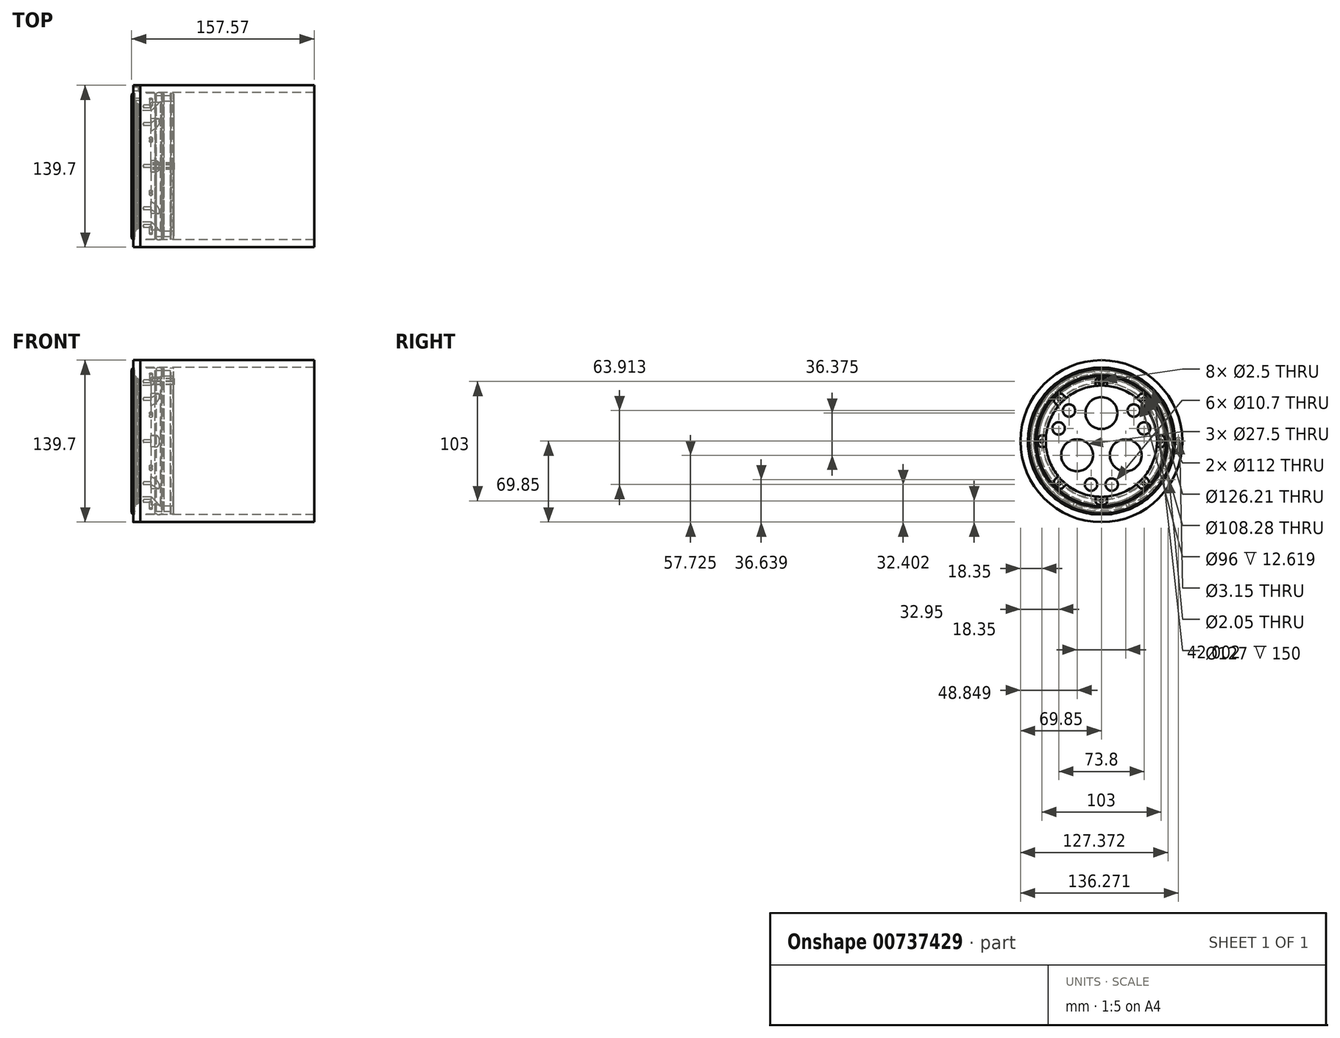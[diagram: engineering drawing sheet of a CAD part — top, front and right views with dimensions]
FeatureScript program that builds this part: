
annotation { "Feature Type Name" : "Feature", "Feature Type Description" : "" }
export const myFeature = defineFeature(function(context is Context, id is Id, definition is map)
    precondition{}
    {
        {
            assignVariable(context, id + "F0", {"name" : "M3_Helicoil_Drill_Depth", "anyValue" : 6.5});
        }
        {
            var Q0;
            Q0=qCreatedBy(makeId("Front.planeOp"),FACE);
            var sketch = newSketch(context, id + "F1", { "sketchPlane" : qUnion([Q0])});
            skLineSegment(sketch, "E0", {"start": v(0, 69.85) * mm, "end": v(6.25, 69.85) * mm});
            skLineSegment(sketch, "E1", {"start": v(6.25, 69.85) * mm, "end": v(6.25, 63) * mm});
            skLineSegment(sketch, "E2", {"start": v(6.25, 63) * mm, "end": v(35, 63) * mm, "construction": true});
            skLineSegment(sketch, "E3", {"start": v(35, 63) * mm, "end": v(35, 56) * mm});
            skLineSegment(sketch, "E4", {"start": v(35, 56) * mm, "end": v(23.5, 56) * mm});
            skLineSegment(sketch, "E5", {"start": v(23.5, 56) * mm, "end": v(15.5, 48) * mm});
            skLineSegment(sketch, "E6", {"start": v(15.5, 48) * mm, "end": v(2.38, 48) * mm});
            skLineSegment(sketch, "E7", {"start": v(2.38, 48) * mm, "end": v(2.38, 56) * mm, "construction": true});
            skLineSegment(sketch, "E8", {"start": v(2.38, 56) * mm, "end": v(0, 56) * mm});
            skLineSegment(sketch, "E9", {"start": v(0, 56) * mm, "end": v(0, 69.85) * mm, "construction": true});
            skLineSegment(sketch, "E10", {"start": v(6.25, 63) * mm, "end": v(19, 63) * mm});
            skLineSegment(sketch, "E11", {"start": v(19, 63) * mm, "end": v(19, 60.83) * mm});
            skLineSegment(sketch, "E12", {"start": v(19, 60.83) * mm, "end": v(24.54, 60.83) * mm});
            skLineSegment(sketch, "E13", {"start": v(24.54, 60.83) * mm, "end": v(24.54, 63) * mm});
            skLineSegment(sketch, "E14", {"start": v(24.54, 63) * mm, "end": v(25.54, 63) * mm});
            skLineSegment(sketch, "E15", {"start": v(25.54, 63) * mm, "end": v(25.54, 56) * mm, "construction": true});
            skLineSegment(sketch, "E16.MirrorCS", {"start": v(26.54, 63) * mm, "end": v(25.54, 63) * mm});
            skLineSegment(sketch, "E17.MirrorCS", {"start": v(26.54, 60.83) * mm, "end": v(26.54, 63) * mm});
            skLineSegment(sketch, "E18.MirrorCS", {"start": v(32.07, 60.83) * mm, "end": v(26.54, 60.83) * mm});
            skLineSegment(sketch, "E19.MirrorCS", {"start": v(32.07, 63) * mm, "end": v(32.07, 60.83) * mm});
            skLineSegment(sketch, "E20", {"start": v(32.07, 63) * mm, "end": v(35, 63) * mm});
            skLineSegment(sketch, "E21", {"start": v(0, 0) * mm, "end": v(57.37, 0) * mm, "construction": true});
            skLineSegment(sketch, "E22", {"start": v(0, 69.85) * mm, "end": v(0, 63.1) * mm});
            skLineSegment(sketch, "E23", {"start": v(0, 63.1) * mm, "end": v(1.32, 63.1) * mm});
            skLineSegment(sketch, "E24", {"start": v(1.32, 63.1) * mm, "end": v(1.32, 58.53) * mm});
            skLineSegment(sketch, "E25", {"start": v(1.32, 58.53) * mm, "end": v(0, 58.53) * mm});
            skLineSegment(sketch, "E26", {"start": v(0, 58.53) * mm, "end": v(0, 56) * mm});
            skLineSegment(sketch, "E27", {"start": v(2.38, 48) * mm, "end": v(2.38, 50.63) * mm});
            skLineSegment(sketch, "E28", {"start": v(2.38, 50.63) * mm, "end": v(4.31, 50.63) * mm});
            skLineSegment(sketch, "E29", {"start": v(4.31, 50.63) * mm, "end": v(4.31, 54.14) * mm});
            skLineSegment(sketch, "E30", {"start": v(4.31, 54.14) * mm, "end": v(2.38, 54.14) * mm});
            skLineSegment(sketch, "E31", {"start": v(2.38, 54.14) * mm, "end": v(2.38, 56) * mm});
            skLineSegment(sketch, "E32", {"start": v(-1, 89.78) * mm, "end": v(37.1, 89.78) * mm, "construction": true});
            skSolve(sketch);
        }
        {
            var Q0;
            Q0=qSketchRegion(id+"F1",true);
            var Q1;
            Q1=sQuery(id+"F1.wireOp",EDGE,"E21");
            revolve(context, id + "F2", {"entities" : qUnion([Q0]), "axis" : qUnion([Q1]), "revolveType" : RevolveType.FULL});
        }
        {
            var Q0;
            Q0=makeQuery(id+"F2.opRevolve","SWEPT_FACE",FACE,{"disambiguationData":[OSD([sQuery(id+"F1.wireOp",EDGE,"E1")])]});
            var sketch = newSketch(context, id + "F3", { "sketchPlane" : qUnion([Q0])});
            skCircle(sketch, "E33", {"center": v(0, 0) * mm, "radius": 66.42 * mm, "construction": true});
            skLineSegment(sketch, "E34", {"start": v(0, 0) * mm, "end": v(66.42, 0) * mm, "construction": true});
            skLineSegment(sketch, "E35.1.0", {"start": v(0, 0) * mm, "end": v(57.52, 33.21) * mm, "construction": true});
            skLineSegment(sketch, "E35.2.0", {"start": v(0, 0) * mm, "end": v(33.21, 57.52) * mm, "construction": true});
            skLineSegment(sketch, "E36.1.3.0", {"start": v(0, 0) * mm, "end": v(0, 66.42) * mm, "construction": true});
            skLineSegment(sketch, "E36.1.4.0", {"start": v(0, 0) * mm, "end": v(-33.21, 57.52) * mm, "construction": true});
            skLineSegment(sketch, "E36.1.5.0", {"start": v(0, 0) * mm, "end": v(-57.52, 33.21) * mm, "construction": true});
            skLineSegment(sketch, "E37.1.6.0", {"start": v(0, 0) * mm, "end": v(-66.42, 0) * mm, "construction": true});
            skLineSegment(sketch, "E37.1.7.0", {"start": v(0, 0) * mm, "end": v(-57.52, -33.21) * mm, "construction": true});
            skLineSegment(sketch, "E38.1.8.0", {"start": v(0, 0) * mm, "end": v(-33.21, -57.52) * mm, "construction": true});
            skLineSegment(sketch, "E38.1.9.0", {"start": v(0, 0) * mm, "end": v(0, -66.42) * mm, "construction": true});
            skLineSegment(sketch, "E38.1.10.0", {"start": v(0, 0) * mm, "end": v(33.21, -57.52) * mm, "construction": true});
            skLineSegment(sketch, "E38.1.11.0", {"start": v(0, 0) * mm, "end": v(57.52, -33.21) * mm, "construction": true});
            skLineSegment(sketch, "E39", {"start": v(69.85, 0) * mm, "end": v(63, 0) * mm, "construction": true});
            skSolve(sketch);
        }
        {
            var Q0;
            Q0=qCreatedBy(makeId("Top.planeOp"),FACE);
            var Q1;
            Q1=sQuery(id+"F1.wireOp",VERTEX,"E10.end");
            cPlane(context, id + "F4", {"entities" : qUnion([Q0, Q1]), "cplaneType" : CPlaneType.PLANE_POINT, "offset" : 150 * mm, "width" : 150 * mm, "height" : 150 * mm});
        }
        {
            var Q0;
            Q0=qCreatedBy(id+"F4.planeOp",FACE);
            var sketch = newSketch(context, id + "F5", { "sketchPlane" : qUnion([Q0])});
            skPoint(sketch, "E40", {"position": v(15.25, 0) * mm});
            skLineSegment(sketch, "E41.0", {"start": v(6.25, -69.85) * mm, "end": v(6.25, 69.85) * mm, "construction": true});
            skLineSegment(sketch, "E41.1", {"start": v(19, -63) * mm, "end": v(19, 63) * mm, "construction": true});
            skLineSegment(sketch, "E42", {"start": v(6.25, 0) * mm, "end": v(19, 0) * mm, "construction": true});
            skCircle(sketch, "E43", {"center": v(15.25, 0) * mm, "radius": 1.5 * mm, "construction": true});
            skCircle(sketch, "E44", {"center": v(15.25, 0) * mm, "radius": 2.75 * mm, "construction": true});
            skSolve(sketch);
        }
        {
            var Q0;
            Q0=makeQuery(id+"F2.opRevolve","SWEPT_EDGE",EDGE,{"disambiguationData":[OSD([sQuery(id+"F1.wireOp",EDGE,"E3"),sQuery(id+"F1.wireOp",EDGE,"E20")])]});
            chamfer(context, id + "F6", {"entities" : qUnion([Q0]), "chamferType" : ChamferType.OFFSET_ANGLE, "width" : 2 * mm, "oppositeDirection" : false, "angle" : 10 * degree, "tangentPropagation" : true});
        }
        {
            var Q0;
            Q0=makeQuery(id+"F2.opRevolve","SWEPT_EDGE",EDGE,{"disambiguationData":[OSD([sQuery(id+"F1.wireOp",EDGE,"E8"),sQuery(id+"F1.wireOp",EDGE,"E26")])]});
            var Q1;
            Q1=makeQuery(id+"F2.opRevolve","SWEPT_EDGE",EDGE,{"disambiguationData":[OSD([sQuery(id+"F1.wireOp",EDGE,"E6"),sQuery(id+"F1.wireOp",EDGE,"E27")])]});
            chamfer(context, id + "F7", {"entities" : qUnion([Q0, Q1]), "width" : .5 * mm, "tangentPropagation" : true});
        }
        {
            var Q0;
            Q0=makeQuery(id+"F2.opRevolve","SWEPT_EDGE",EDGE,{"disambiguationData":[OSD([sQuery(id+"F1.wireOp",EDGE,"E3"),sQuery(id+"F1.wireOp",EDGE,"E4")])]});
            chamfer(context, id + "F8", {"entities" : qUnion([Q0]), "width" : 1 * mm, "tangentPropagation" : true});
        }
        {
            var Q0;
            Q0=makeQuery(id+"F2.opRevolve","SWEPT_FACE",FACE,{"disambiguationData":[OSD([sQuery(id+"F1.wireOp",EDGE,"E24")])]});
            fillet(context, id + "F9", {"entities" : qUnion([Q0]), "radius" : 0.2 * mm, "tangentPropagation" : true, "allowEdgeOverflow" : false});
        }
        {
            var Q0;
            Q0=makeQuery(id+"F2.opRevolve","SWEPT_FACE",FACE,{"disambiguationData":[OSD([sQuery(id+"F1.wireOp",EDGE,"E29")])]});
            fillet(context, id + "F10", {"entities" : qUnion([Q0]), "radius" : 0.2 * mm, "allowEdgeOverflow" : false});
        }
        {
            var Q0;
            Q0=makeQuery(id+"F2.opRevolve","SWEPT_FACE",FACE,{"disambiguationData":[OSD([sQuery(id+"F1.wireOp",EDGE,"E18.MirrorCS")])]});
            var Q1;
            Q1=makeQuery(id+"F2.opRevolve","SWEPT_FACE",FACE,{"disambiguationData":[OSD([sQuery(id+"F1.wireOp",EDGE,"E12")])]});
            fillet(context, id + "F11", {"entities" : qUnion([Q0, Q1]), "radius" : 0.2 * mm, "tangentPropagation" : true, "allowEdgeOverflow" : false});
        }
        {
            var Q0;
            Q0=makeQuery(id+"F2.opRevolve","SWEPT_EDGE",EDGE,{"disambiguationData":[OSD([sQuery(id+"F1.wireOp",EDGE,"E10"),sQuery(id+"F1.wireOp",EDGE,"E11")])]});
            var Q1;
            Q1=makeQuery(id+"F2.opRevolve","SWEPT_EDGE",EDGE,{"disambiguationData":[OSD([sQuery(id+"F1.wireOp",EDGE,"E13"),sQuery(id+"F1.wireOp",EDGE,"E14")])]});
            var Q2;
            Q2=makeQuery(id+"F2.opRevolve","SWEPT_EDGE",EDGE,{"disambiguationData":[OSD([sQuery(id+"F1.wireOp",EDGE,"E16.MirrorCS"),sQuery(id+"F1.wireOp",EDGE,"E17.MirrorCS")])]});
            var Q3;
            Q3=makeQuery(id+"F2.opRevolve","SWEPT_EDGE",EDGE,{"disambiguationData":[OSD([sQuery(id+"F1.wireOp",EDGE,"E19.MirrorCS"),sQuery(id+"F1.wireOp",EDGE,"E20")])]});
            var Q4;
            Q4=makeQuery(id+"F2.opRevolve","SWEPT_EDGE",EDGE,{"disambiguationData":[OSD([sQuery(id+"F1.wireOp",EDGE,"E0"),sQuery(id+"F1.wireOp",EDGE,"E1")])]});
            var Q5;
            Q5=makeQuery(id+"F2.opRevolve","SWEPT_EDGE",EDGE,{"disambiguationData":[OSD([sQuery(id+"F1.wireOp",EDGE,"E0"),sQuery(id+"F1.wireOp",EDGE,"E22")])]});
            var Q6;
            Q6=makeQuery(id+"F2.opRevolve","SWEPT_EDGE",EDGE,{"disambiguationData":[OSD([sQuery(id+"F1.wireOp",EDGE,"E1"),sQuery(id+"F1.wireOp",EDGE,"E10")])]});
            var Q7;
            Q7=makeQuery(id+"F2.opRevolve","SWEPT_EDGE",EDGE,{"disambiguationData":[OSD([sQuery(id+"F1.wireOp",EDGE,"E22"),sQuery(id+"F1.wireOp",EDGE,"E23")])]});
            var Q8;
            Q8=makeQuery(id+"F2.opRevolve","SWEPT_EDGE",EDGE,{"disambiguationData":[OSD([sQuery(id+"F1.wireOp",EDGE,"E25"),sQuery(id+"F1.wireOp",EDGE,"E26")])]});
            var Q9;
            Q9=makeQuery(id+"F2.opRevolve","SWEPT_EDGE",EDGE,{"disambiguationData":[OSD([sQuery(id+"F1.wireOp",EDGE,"E30"),sQuery(id+"F1.wireOp",EDGE,"E31")])]});
            var Q10;
            Q10=makeQuery(id+"F2.opRevolve","SWEPT_EDGE",EDGE,{"disambiguationData":[OSD([sQuery(id+"F1.wireOp",EDGE,"E27"),sQuery(id+"F1.wireOp",EDGE,"E28")])]});
            var Q11;
            {var subQ0=sQuery(id+"F1.wireOp",EDGE,"E3");Q11=makeQuery(id+"F6.opChamfer","BLEND_EDGE",EDGE,{"blendedFrom":[makeQuery(id+"F2.opRevolve","SWEPT_EDGE",EDGE,{"disambiguationData":[OSD([subQ0,sQuery(id+"F1.wireOp",EDGE,"E20")])]}),makeQuery(id+"F2.opRevolve","SWEPT_FACE",FACE,{"disambiguationData":[OSD([subQ0])]})],"blendedInto":[makeQuery(id+"F2.opRevolve","SWEPT_FACE",FACE,{"disambiguationData":[OSD([subQ0])]})]});}
            var Q12;
            Q12=makeQuery(id+"F2.opRevolve","SWEPT_EDGE",EDGE,{"disambiguationData":[OSD([sQuery(id+"F1.wireOp",EDGE,"E8"),sQuery(id+"F1.wireOp",EDGE,"E31")])]});
            chamfer(context, id + "F12", {"entities" : qUnion([Q0, Q1, Q2, Q3, Q4, Q5, Q6, Q7, Q8, Q9, Q10, Q11, Q12]), "width" : 0.25 * mm, "tangentPropagation" : true});
        }
        {
            var Q0;
            Q0=sQuery(id+"F3.wireOp",VERTEX,"E34.end");
            var Q1;
            Q1=makeQuery(id+"F2.opRevolve","SWEPT_BODY",BODY,{"disambiguationData":[OSD([sQuery(id+"F1.wireOp",EDGE,"E0"),sQuery(id+"F1.wireOp",EDGE,"E1"),sQuery(id+"F1.wireOp",EDGE,"E3"),sQuery(id+"F1.wireOp",EDGE,"EppfiJ0T-nPKM-5v7P-hZBO-1SXBlnIL5BD0"),sQuery(id+"F1.wireOp",EDGE,"E4"),sQuery(id+"F1.wireOp",EDGE,"E5"),sQuery(id+"F1.wireOp",EDGE,"E6"),sQuery(id+"F1.wireOp",EDGE,"E7"),sQuery(id+"F1.wireOp",EDGE,"E8"),sQuery(id+"F1.wireOp",EDGE,"E9"),sQuery(id+"F1.wireOp",EDGE,"E10"),sQuery(id+"F1.wireOp",EDGE,"E11"),sQuery(id+"F1.wireOp",EDGE,"E12"),sQuery(id+"F1.wireOp",EDGE,"E13"),sQuery(id+"F1.wireOp",EDGE,"E14"),sQuery(id+"F1.wireOp",EDGE,"E16.MirrorCS"),sQuery(id+"F1.wireOp",EDGE,"E17.MirrorCS"),sQuery(id+"F1.wireOp",EDGE,"E18.MirrorCS"),sQuery(id+"F1.wireOp",EDGE,"E19.MirrorCS"),sQuery(id+"F1.wireOp",EDGE,"E20")])]});
            hole(context, id + "F13", {"style" : HoleStyle.C_SINK, "endStyle" : HoleEndStyle.THROUGH, "holeDiameter" : 3.15 * mm, "cSinkDiameter" : 6.2 * mm, "cSinkAngle" : 90 * degree, "locations" : qUnion([Q0]), "scope" : qUnion([Q1]), "tappedDepth" : 12 * mm, "tapClearance" : 3});
        }
        {
            var Q0;
            Q0=sQuery(id+"F3.wireOp",VERTEX,"E38.1.11.0.end");
            var Q1;
            Q1=makeQuery(id+"F2.opRevolve","SWEPT_BODY",BODY,{"disambiguationData":[OSD([sQuery(id+"F1.wireOp",EDGE,"E0"),sQuery(id+"F1.wireOp",EDGE,"E1"),sQuery(id+"F1.wireOp",EDGE,"E3"),sQuery(id+"F1.wireOp",EDGE,"EppfiJ0T-nPKM-5v7P-hZBO-1SXBlnIL5BD0"),sQuery(id+"F1.wireOp",EDGE,"E4"),sQuery(id+"F1.wireOp",EDGE,"E5"),sQuery(id+"F1.wireOp",EDGE,"E6"),sQuery(id+"F1.wireOp",EDGE,"E7"),sQuery(id+"F1.wireOp",EDGE,"E8"),sQuery(id+"F1.wireOp",EDGE,"E9"),sQuery(id+"F1.wireOp",EDGE,"E10"),sQuery(id+"F1.wireOp",EDGE,"E11"),sQuery(id+"F1.wireOp",EDGE,"E12"),sQuery(id+"F1.wireOp",EDGE,"E13"),sQuery(id+"F1.wireOp",EDGE,"E14"),sQuery(id+"F1.wireOp",EDGE,"E16.MirrorCS"),sQuery(id+"F1.wireOp",EDGE,"E17.MirrorCS"),sQuery(id+"F1.wireOp",EDGE,"E18.MirrorCS"),sQuery(id+"F1.wireOp",EDGE,"E19.MirrorCS"),sQuery(id+"F1.wireOp",EDGE,"E20")])]});
            hole(context, id + "F14", {"style" : HoleStyle.SIMPLE, "endStyle" : HoleEndStyle.THROUGH, "holeDiameter" : (2.5 - .45) * mm, "locations" : qUnion([Q0]), "scope" : qUnion([Q1]), "isTappedThrough" : true});
        }
        {
            var Q0;
            Q0=makeQuery(id+"F2.opRevolve","SWEPT_FACE",FACE,{"disambiguationData":[OSD([sQuery(id+"F1.wireOp",EDGE,"E31")])]});
            var sketch = newSketch(context, id + "F15", { "sketchPlane" : qUnion([Q0])});
            skCircle(sketch, "E45", {"center": v(0, 0) * mm, "radius": 55.9 * mm});
            skCircle(sketch, "E46.0", {"center": v(0, 0) * mm, "radius": 56 * mm, "construction": true});
            skCircle(sketch, "E47", {"center": v(0, 24.25) * mm, "radius": 19.05 * mm, "construction": true});
            skCircle(sketch, "E48", {"center": v(-21, -12.12) * mm, "radius": 19.05 * mm, "construction": true});
            skCircle(sketch, "E49", {"center": v(0, 0) * mm, "radius": 24.25 * mm, "construction": true});
            skCircle(sketch, "E50", {"center": v(21, -12.12) * mm, "radius": 19.05 * mm, "construction": true});
            skLineSegment(sketch, "E51", {"start": v(-21, -12.13) * mm, "end": v(0, 0) * mm, "construction": true});
            skLineSegment(sketch, "E52", {"start": v(21, -12.12) * mm, "end": v(0, 0) * mm, "construction": true});
            skLineSegment(sketch, "E53", {"start": v(0, 24.25) * mm, "end": v(0, 0) * mm, "construction": true});
            skCircle(sketch, "E54", {"center": v(0, 24.25) * mm, "radius": 13.75 * mm});
            skCircle(sketch, "E55", {"center": v(-21, -12.12) * mm, "radius": 13.75 * mm});
            skCircle(sketch, "E56", {"center": v(21, -12.12) * mm, "radius": 13.75 * mm});
            skCircle(sketch, "E57", {"center": v(-36.9, 10.98) * mm, "radius": 8.25 * mm, "construction": true});
            skCircle(sketch, "E58", {"center": v(0, 0) * mm, "radius": 38.5 * mm, "construction": true});
            skCircle(sketch, "E59", {"center": v(-27.96, 26.46) * mm, "radius": 8.25 * mm, "construction": true});
            skLineSegment(sketch, "E60", {"start": v(0, 0) * mm, "end": v(-33.34, 19.25) * mm, "construction": true});
            skLineSegment(sketch, "E61", {"start": v(0, 0) * mm, "end": v(33.34, 19.25) * mm, "construction": true});
            skLineSegment(sketch, "E62", {"start": v(0, 0) * mm, "end": v(0, -38.5) * mm, "construction": true});
            skCircle(sketch, "E63", {"center": v(-27.96, 26.46) * mm, "radius": 5.35 * mm});
            skCircle(sketch, "E64", {"center": v(-36.9, 10.98) * mm, "radius": 5.35 * mm});
            skCircle(sketch, "E65.1.0", {"center": v(8.94, -37.45) * mm, "radius": 5.35 * mm});
            skCircle(sketch, "E65.1.1", {"center": v(8.94, -37.45) * mm, "radius": 8.25 * mm, "construction": true});
            skCircle(sketch, "E65.1.2", {"center": v(-8.94, -37.45) * mm, "radius": 5.35 * mm});
            skCircle(sketch, "E65.1.3", {"center": v(-8.94, -37.45) * mm, "radius": 8.25 * mm, "construction": true});
            skCircle(sketch, "E65.2.0", {"center": v(27.96, 26.46) * mm, "radius": 5.35 * mm});
            skCircle(sketch, "E65.2.1", {"center": v(27.96, 26.46) * mm, "radius": 8.25 * mm, "construction": true});
            skCircle(sketch, "E65.2.2", {"center": v(36.9, 10.98) * mm, "radius": 5.35 * mm});
            skCircle(sketch, "E65.2.3", {"center": v(36.9, 10.98) * mm, "radius": 8.25 * mm, "construction": true});
            skSolve(sketch);
        }
        {
            var Q0;
            Q0=qSketchRegion(id+"F15",true);
            extrude(context, id + "F16", {"entities" : qUnion([Q0]), "depth" : 3 / 406.4 * mm});
        }
        {
            var Q0;
            Q0=qCreatedBy(makeId("Top.planeOp"),FACE);
            cPlane(context, id + "F17", {"entities" : qUnion([Q0]), "cplaneType" : CPlaneType.OFFSET, "offset" : 5.5 / 50.8 * mm, "width" : 150 * mm, "height" : 150 * mm});
        }
        {
            var Q0;
            Q0=qCreatedBy(makeId("Front.planeOp"),FACE);
            var sketch = newSketch(context, id + "F18", { "sketchPlane" : qUnion([Q0])});
            skLineSegment(sketch, "E66", {"start": v(15.5, -48) * mm, "end": v(2.88, -48) * mm});
            skLineSegment(sketch, "E67", {"start": v(2.88, 48) * mm, "end": v(15.5, 48) * mm});
            skLineSegment(sketch, "E68", {"start": v(15.5, 48) * mm, "end": v(23.5, 56) * mm});
            skLineSegment(sketch, "E69", {"start": v(23.5, -56) * mm, "end": v(15.5, -48) * mm});
            skLineSegment(sketch, "E70", {"start": v(34, -56) * mm, "end": v(23.5, -56) * mm});
            skLineSegment(sketch, "E71", {"start": v(23.5, 56) * mm, "end": v(34, 56) * mm});
            skLineSegment(sketch, "E72", {"start": v(34, 56) * mm, "end": v(35, 57) * mm});
            skLineSegment(sketch, "E73", {"start": v(35, -57) * mm, "end": v(34, -56) * mm});
            skLineSegment(sketch, "E74", {"start": v(35, 57) * mm, "end": v(35, 62.43) * mm});
            skLineSegment(sketch, "E75", {"start": v(35, -62.43) * mm, "end": v(35, -57) * mm});
            skLineSegment(sketch, "E76", {"start": v(34.8, -62.68) * mm, "end": v(35, -62.43) * mm});
            skLineSegment(sketch, "E77", {"start": v(35, 62.43) * mm, "end": v(34.8, 62.68) * mm});
            skLineSegment(sketch, "E78", {"start": v(33, -63) * mm, "end": v(34.8, -62.68) * mm});
            skLineSegment(sketch, "E79", {"start": v(34.8, 62.68) * mm, "end": v(33, 63) * mm});
            skLineSegment(sketch, "E80", {"start": v(32.32, -63) * mm, "end": v(33, -63) * mm});
            skLineSegment(sketch, "E81", {"start": v(33, 63) * mm, "end": v(32.32, 63) * mm});
            skLineSegment(sketch, "E82", {"start": v(32.32, 63) * mm, "end": v(32.07, 62.74) * mm});
            skLineSegment(sketch, "E83", {"start": v(32.07, -62.74) * mm, "end": v(32.32, -63) * mm});
            skLineSegment(sketch, "E84", {"start": v(32.07, 61.03) * mm, "end": v(32.07, 62.74) * mm});
            skLineSegment(sketch, "E85", {"start": v(32.07, -62.74) * mm, "end": v(32.07, -61.03) * mm});
            skArc(sketch, "E86", {"start": v(31.87, 60.83) * mm, "mid": v(32.02, 60.9) * mm, "end": v(32.07, 61.03) * mm});
            skArc(sketch, "E87", {"start": v(32.07, -61.03) * mm, "mid": v(32.02, -60.9) * mm, "end": v(31.87, -60.83) * mm});
            skLineSegment(sketch, "E88", {"start": v(31.87, -60.83) * mm, "end": v(26.74, -60.83) * mm});
            skLineSegment(sketch, "E89", {"start": v(26.74, 60.83) * mm, "end": v(31.87, 60.83) * mm});
            skArc(sketch, "E90", {"start": v(26.74, -60.83) * mm, "mid": v(26.6, -60.9) * mm, "end": v(26.54, -61.03) * mm});
            skArc(sketch, "E91", {"start": v(26.54, 61.03) * mm, "mid": v(26.6, 60.9) * mm, "end": v(26.74, 60.83) * mm});
            skLineSegment(sketch, "E92", {"start": v(26.54, -61.03) * mm, "end": v(26.54, -62.74) * mm});
            skLineSegment(sketch, "E93", {"start": v(26.54, 62.74) * mm, "end": v(26.54, 61.03) * mm});
            skLineSegment(sketch, "E94", {"start": v(26.29, -63) * mm, "end": v(26.54, -62.74) * mm});
            skLineSegment(sketch, "E95", {"start": v(26.54, 62.74) * mm, "end": v(26.29, 63) * mm});
            skLineSegment(sketch, "E96", {"start": v(26.29, -63) * mm, "end": v(24.79, -63) * mm});
            skLineSegment(sketch, "E97", {"start": v(24.79, 63) * mm, "end": v(26.29, 63) * mm});
            skLineSegment(sketch, "E98", {"start": v(24.79, 63) * mm, "end": v(24.54, 62.74) * mm});
            skLineSegment(sketch, "E99", {"start": v(24.54, -62.74) * mm, "end": v(24.79, -63) * mm});
            skLineSegment(sketch, "E100", {"start": v(24.54, -61.03) * mm, "end": v(24.54, -62.74) * mm});
            skLineSegment(sketch, "E101", {"start": v(24.54, 62.74) * mm, "end": v(24.54, 61.03) * mm});
            skArc(sketch, "E102", {"start": v(24.54, -61.03) * mm, "mid": v(24.48, -60.9) * mm, "end": v(24.34, -60.83) * mm});
            skArc(sketch, "E103", {"start": v(24.34, 60.83) * mm, "mid": v(24.48, 60.9) * mm, "end": v(24.54, 61.03) * mm});
            skLineSegment(sketch, "E104", {"start": v(19.2, -60.83) * mm, "end": v(24.34, -60.83) * mm});
            skLineSegment(sketch, "E105", {"start": v(24.34, 60.83) * mm, "end": v(19.2, 60.83) * mm});
            skArc(sketch, "E106", {"start": v(19, 61.03) * mm, "mid": v(19.06, 60.9) * mm, "end": v(19.2, 60.83) * mm});
            skArc(sketch, "E107", {"start": v(19.2, -60.83) * mm, "mid": v(19.06, -60.9) * mm, "end": v(19, -61.03) * mm});
            skLineSegment(sketch, "E108", {"start": v(19, 61.03) * mm, "end": v(19, 62.74) * mm});
            skLineSegment(sketch, "E109", {"start": v(19, -62.74) * mm, "end": v(19, -61.03) * mm});
            skLineSegment(sketch, "E110", {"start": v(18.75, -63) * mm, "end": v(19, -62.74) * mm});
            skLineSegment(sketch, "E111", {"start": v(19, 62.74) * mm, "end": v(18.75, 63) * mm});
            skLineSegment(sketch, "E112", {"start": v(14.05, 63) * mm, "end": v(6.5, 63) * mm});
            skLineSegment(sketch, "E113", {"start": v(6.5, -63) * mm, "end": v(18.75, -63) * mm});
            skLineSegment(sketch, "E114", {"start": v(18.75, 63) * mm, "end": v(16.45, 63) * mm});
            skLineSegment(sketch, "E115", {"start": v(6.5, -63) * mm, "end": v(6.25, -63.24) * mm});
            skLineSegment(sketch, "E116", {"start": v(6.25, 63.24) * mm, "end": v(6.5, 63) * mm});
            skLineSegment(sketch, "E117", {"start": v(6.25, -65.4) * mm, "end": v(6.25, -63.24) * mm});
            skLineSegment(sketch, "E118", {"start": v(6.25, 63.24) * mm, "end": v(6.25, 65.4) * mm});
            skLineSegment(sketch, "E119", {"start": v(6.25, 67.45) * mm, "end": v(6.25, 69.6) * mm});
            skLineSegment(sketch, "E120", {"start": v(6.25, -69.6) * mm, "end": v(6.25, -67.45) * mm});
            skLineSegment(sketch, "E121", {"start": v(6, -69.85) * mm, "end": v(6.25, -69.6) * mm});
            skLineSegment(sketch, "E122", {"start": v(6.25, 69.6) * mm, "end": v(6, 69.85) * mm});
            skLineSegment(sketch, "E123", {"start": v(0.25, -69.85) * mm, "end": v(6, -69.85) * mm});
            skLineSegment(sketch, "E124", {"start": v(6, 69.85) * mm, "end": v(0.25, 69.85) * mm});
            skLineSegment(sketch, "E125", {"start": v(0.25, 69.85) * mm, "end": v(0, 69.6) * mm});
            skLineSegment(sketch, "E126", {"start": v(0, -69.6) * mm, "end": v(0.25, -69.85) * mm});
            skLineSegment(sketch, "E127", {"start": v(0, -65.4) * mm, "end": v(0, -63.36) * mm});
            skLineSegment(sketch, "E128", {"start": v(0, 63.36) * mm, "end": v(0, 65.4) * mm});
            skLineSegment(sketch, "E129", {"start": v(0, 67.45) * mm, "end": v(0, 69.6) * mm});
            skLineSegment(sketch, "E130", {"start": v(0, -69.6) * mm, "end": v(0, -67.45) * mm});
            skLineSegment(sketch, "E131", {"start": v(0.25, -63.1) * mm, "end": v(0, -63.36) * mm});
            skLineSegment(sketch, "E132", {"start": v(0, 63.36) * mm, "end": v(0.25, 63.1) * mm});
            skLineSegment(sketch, "E133", {"start": v(0.25, -63.1) * mm, "end": v(1.12, -63.1) * mm});
            skLineSegment(sketch, "E134", {"start": v(1.12, 63.1) * mm, "end": v(0.25, 63.1) * mm});
            skArc(sketch, "E135", {"start": v(1.32, 62.9) * mm, "mid": v(1.26, 63.05) * mm, "end": v(1.12, 63.1) * mm});
            skArc(sketch, "E136", {"start": v(1.12, -63.1) * mm, "mid": v(1.26, -63.05) * mm, "end": v(1.32, -62.9) * mm});
            skLineSegment(sketch, "E137", {"start": v(1.32, 58.73) * mm, "end": v(1.32, 62.9) * mm});
            skLineSegment(sketch, "E138", {"start": v(1.32, -62.9) * mm, "end": v(1.32, -58.73) * mm});
            skArc(sketch, "E139", {"start": v(1.12, 58.53) * mm, "mid": v(1.26, 58.6) * mm, "end": v(1.32, 58.73) * mm});
            skArc(sketch, "E140", {"start": v(1.32, -58.73) * mm, "mid": v(1.26, -58.6) * mm, "end": v(1.12, -58.53) * mm});
            skLineSegment(sketch, "E141", {"start": v(1.12, -58.53) * mm, "end": v(0.25, -58.53) * mm});
            skLineSegment(sketch, "E142", {"start": v(0.25, 58.53) * mm, "end": v(1.12, 58.53) * mm});
            skLineSegment(sketch, "E143", {"start": v(0.25, 58.53) * mm, "end": v(0, 58.28) * mm});
            skLineSegment(sketch, "E144", {"start": v(0, -58.28) * mm, "end": v(0.25, -58.53) * mm});
            skLineSegment(sketch, "E145", {"start": v(0, 56.5) * mm, "end": v(0, 58.28) * mm});
            skLineSegment(sketch, "E146", {"start": v(0, -58.28) * mm, "end": v(0, -56.5) * mm});
            skLineSegment(sketch, "E147", {"start": v(0.5, -56) * mm, "end": v(0, -56.5) * mm});
            skLineSegment(sketch, "E148", {"start": v(0, 56.5) * mm, "end": v(0.5, 56) * mm});
            skLineSegment(sketch, "E149", {"start": v(2.38, -56) * mm, "end": v(0.5, -56) * mm});
            skLineSegment(sketch, "E150", {"start": v(2.38, -54.4) * mm, "end": v(2.38, -56) * mm});
            skLineSegment(sketch, "E151", {"start": v(2.63, -54.14) * mm, "end": v(2.38, -54.4) * mm});
            skLineSegment(sketch, "E152", {"start": v(2.38, 54.4) * mm, "end": v(2.63, 54.14) * mm});
            skLineSegment(sketch, "E153", {"start": v(4.11, -54.14) * mm, "end": v(2.63, -54.14) * mm});
            skLineSegment(sketch, "E154", {"start": v(2.63, 54.14) * mm, "end": v(4.11, 54.14) * mm});
            skArc(sketch, "E155", {"start": v(4.11, -54.14) * mm, "mid": v(4.25, -54.08) * mm, "end": v(4.31, -53.94) * mm});
            skArc(sketch, "E156", {"start": v(4.31, 53.94) * mm, "mid": v(4.25, 54.08) * mm, "end": v(4.11, 54.14) * mm});
            skLineSegment(sketch, "E157", {"start": v(4.31, -50.83) * mm, "end": v(4.31, -53.94) * mm});
            skLineSegment(sketch, "E158", {"start": v(4.31, 53.94) * mm, "end": v(4.31, 50.83) * mm});
            skArc(sketch, "E159", {"start": v(4.31, -50.83) * mm, "mid": v(4.25, -50.7) * mm, "end": v(4.11, -50.63) * mm});
            skArc(sketch, "E160", {"start": v(4.11, 50.63) * mm, "mid": v(4.25, 50.7) * mm, "end": v(4.31, 50.83) * mm});
            skLineSegment(sketch, "E161", {"start": v(2.63, -50.63) * mm, "end": v(4.11, -50.63) * mm});
            skLineSegment(sketch, "E162", {"start": v(4.11, 50.63) * mm, "end": v(2.63, 50.63) * mm});
            skLineSegment(sketch, "E163", {"start": v(2.63, 50.63) * mm, "end": v(2.38, 50.38) * mm});
            skLineSegment(sketch, "E164", {"start": v(2.38, -50.38) * mm, "end": v(2.63, -50.63) * mm});
            skLineSegment(sketch, "E165", {"start": v(2.38, -48.5) * mm, "end": v(2.38, -50.38) * mm});
            skLineSegment(sketch, "E166", {"start": v(2.38, 50.38) * mm, "end": v(2.38, 48.5) * mm});
            skLineSegment(sketch, "E167", {"start": v(2.88, -48) * mm, "end": v(2.38, -48.5) * mm});
            skLineSegment(sketch, "E168", {"start": v(2.38, 48.5) * mm, "end": v(2.88, 48) * mm});
            skLineSegment(sketch, "E169", {"start": v(2.13, -56) * mm, "end": v(0.5, -56) * mm});
            skLineSegment(sketch, "E170", {"start": v(0.5, 56) * mm, "end": v(2.13, 56) * mm});
            skLineSegment(sketch, "E171", {"start": v(2.13, -56) * mm, "end": v(2.38, -55.75) * mm});
            skLineSegment(sketch, "E172", {"start": v(2.38, 55.75) * mm, "end": v(2.13, 56) * mm});
            skLineSegment(sketch, "E173", {"start": v(2.38, -54.4) * mm, "end": v(2.38, -55.75) * mm});
            skLineSegment(sketch, "E174", {"start": v(2.38, 55.75) * mm, "end": v(2.38, 54.4) * mm});
            skLineSegment(sketch, "E175", {"start": v(0, 65.4) * mm, "end": v(0, 67.45) * mm});
            skLineSegment(sketch, "E176", {"start": v(6.25, 65.4) * mm, "end": v(6.25, 67.45) * mm});
            skLineSegment(sketch, "E177", {"start": v(14.05, 63) * mm, "end": v(16.45, 63) * mm});
            skSolve(sketch);
        }
        {
            var Q0;
            Q0=qCreatedBy(makeId("Front.planeOp"),FACE);
            var sketch = newSketch(context, id + "F19", { "sketchPlane" : qUnion([Q0])});
            skLineSegment(sketch, "E178", {"start": v(310.8, -69.85) * mm, "end": v(6, -69.85) * mm, "construction": true});
            skLineSegment(sketch, "E179", {"start": v(6, 69.85) * mm, "end": v(310.8, 69.85) * mm, "construction": true});
            skLineSegment(sketch, "E180", {"start": v(0, -69.85) * mm, "end": v(5.5, -69.85) * mm, "construction": true});
            skLineSegment(sketch, "E181", {"start": v(5.5, 69.85) * mm, "end": v(0, 69.85) * mm, "construction": true});
            skLineSegment(sketch, "E182", {"start": v(310.8, -63.5) * mm, "end": v(6, -63.5) * mm, "construction": true});
            skLineSegment(sketch, "E183", {"start": v(6, 63.5) * mm, "end": v(310.8, 63.5) * mm, "construction": true});
            skLineSegment(sketch, "E184", {"start": v(19.2, -60.83) * mm, "end": v(24.34, -60.83) * mm, "construction": true});
            skLineSegment(sketch, "E185", {"start": v(24.34, 60.83) * mm, "end": v(19.2, 60.83) * mm, "construction": true});
            skLineSegment(sketch, "E186", {"start": v(19, 61.03) * mm, "end": v(19, 63) * mm, "construction": true});
            skLineSegment(sketch, "E187", {"start": v(19, -63) * mm, "end": v(19, -61.03) * mm, "construction": true});
            skLineSegment(sketch, "E188", {"start": v(24.54, -61.03) * mm, "end": v(24.54, -63) * mm, "construction": true});
            skLineSegment(sketch, "E189", {"start": v(24.54, 63) * mm, "end": v(24.54, 61.03) * mm, "construction": true});
            skEllipse(sketch, "E190", {"center": v(22.2, 62.17) * mm, "majorRadius": 2.33 * mm, "minorRadius": 1.33 * mm, "majorAxis": v(1, 0)});
            skLineSegment(sketch, "E191", {"start": v(0, 0) * mm, "end": v(53.93, 0) * mm, "construction": true});
            skLineSegment(sketch, "E192", {"start": v(1.32, 58.73) * mm, "end": v(1.32, 62.9) * mm, "construction": true});
            skLineSegment(sketch, "E193", {"start": v(1.32, -62.9) * mm, "end": v(1.32, -58.73) * mm, "construction": true});
            skLineSegment(sketch, "E194", {"start": v(0, -63.1) * mm, "end": v(1.12, -63.1) * mm, "construction": true});
            skLineSegment(sketch, "E195", {"start": v(1.12, 63.1) * mm, "end": v(0, 63.1) * mm, "construction": true});
            skLineSegment(sketch, "E196", {"start": v(1.12, -58.53) * mm, "end": v(0, -58.53) * mm, "construction": true});
            skLineSegment(sketch, "E197", {"start": v(0, 58.53) * mm, "end": v(1.12, 58.53) * mm, "construction": true});
            skLineSegment(sketch, "E198", {"start": v(2.38, -50.63) * mm, "end": v(4.11, -50.63) * mm, "construction": true});
            skLineSegment(sketch, "E199", {"start": v(4.11, 50.63) * mm, "end": v(2.38, 50.63) * mm, "construction": true});
            skLineSegment(sketch, "E200", {"start": v(4.31, -50.83) * mm, "end": v(4.31, -53.94) * mm, "construction": true});
            skLineSegment(sketch, "E201", {"start": v(4.31, 53.94) * mm, "end": v(4.31, 50.83) * mm, "construction": true});
            skLineSegment(sketch, "E202", {"start": v(4.11, -54.14) * mm, "end": v(2.38, -54.14) * mm, "construction": true});
            skLineSegment(sketch, "E203", {"start": v(2.38, 54.14) * mm, "end": v(4.11, 54.14) * mm, "construction": true});
            skEllipse(sketch, "E204", {"center": v(0, 60.82) * mm, "majorRadius": 2.29 * mm, "minorRadius": 1.32 * mm, "majorAxis": v(0, -1)});
            skLineSegment(sketch, "E205", {"start": v(0, -63.1) * mm, "end": v(1.12, -63.1) * mm});
            skLineSegment(sketch, "E206", {"start": v(1.12, 63.1) * mm, "end": v(0, 63.1) * mm});
            skLineSegment(sketch, "E207", {"start": v(0, 63.1) * mm, "end": v(0, 69.85) * mm});
            skLineSegment(sketch, "E208", {"start": v(0, -69.85) * mm, "end": v(0, -63.1) * mm});
            skLineSegment(sketch, "E209", {"start": v(0, 63.1) * mm, "end": v(0, 58.53) * mm, "construction": true});
            skEllipse(sketch, "E210", {"center": v(3.35, 52.39) * mm, "majorRadius": 1.75 * mm, "minorRadius": 0.97 * mm, "majorAxis": v(0, -1)});
            skPoint(sketch, "E211", {"position": v(4.31, 52.39) * mm});
            skLineSegment(sketch, "E212", {"start": v(2.38, 50.63) * mm, "end": v(2.38, 54.14) * mm, "construction": true});
            skSolve(sketch);
        }
        {
            var Q0;
            Q0=makeQuery(id+"F19.imprint","IMPRINT",FACE,{"disambiguationData":[TD([[makeQuery(id+"F19.imprint","IMPRINT",EDGE,{"derivedFrom":sQuery(id+"F19.wireOp",EDGE,"E190")}),1.0]])]});
            var Q1;
            Q1=makeQuery(id+"F19.imprint","IMPRINT",FACE,{"disambiguationData":[TD([[makeQuery(id+"F19.imprint","IMPRINT",EDGE,{"derivedFrom":sQuery(id+"F19.wireOp",EDGE,"E204")}),1.0]])]});
            var Q2;
            Q2=makeQuery(id+"F19.imprint","IMPRINT",FACE,{"disambiguationData":[TD([[makeQuery(id+"F19.imprint","IMPRINT",EDGE,{"derivedFrom":sQuery(id+"F19.wireOp",EDGE,"E210")}),1.0]])]});
            var Q3;
            Q3=sQuery(id+"F19.wireOp",EDGE,"E190");
            var Q4;
            Q4=sQuery(id+"F19.wireOp",EDGE,"E191");
            revolve(context, id + "F20", {"entities" : qUnion([Q0, Q1, Q2]), "surfaceEntities" : qUnion([Q3]), "axis" : qUnion([Q4]), "revolveType" : RevolveType.FULL});
        }
        {
            var Q0;
            Q0=sQuery(id+"F18.wireOp",VERTEX,"E67.end");
            var Q1;
            Q1=qCreatedBy(makeId("Right.planeOp"),FACE);
            cPlane(context, id + "F21", {"entities" : qUnion([Q0, Q1]), "cplaneType" : CPlaneType.PLANE_POINT, "offset" : 25 * mm, "width" : 150 * mm, "height" : 150 * mm});
        }
        {
            var Q0;
            Q0=qCreatedBy(id+"F21.planeOp",FACE);
            var sketch = newSketch(context, id + "F22", { "sketchPlane" : qUnion([Q0])});
            skCircle(sketch, "E213.0", {"center": v(0, 0) * mm, "radius": 56 * mm, "construction": true});
            skArc(sketch, "E214.0", {"start": v(5, 47.74) * mm, "mid": v(0, 48) * mm, "end": v(-5, 47.74) * mm});
            skLineSegment(sketch, "E215", {"start": v(-5, 47.74) * mm, "end": v(-5, 51.5) * mm});
            skLineSegment(sketch, "E216", {"start": v(-1.5, 55) * mm, "end": v(1.5, 55) * mm});
            skLineSegment(sketch, "E217", {"start": v(5, 51.5) * mm, "end": v(5, 47.74) * mm});
            skLineSegment(sketch, "E218", {"start": v(0, 0) * mm, "end": v(0, 70.4) * mm, "construction": true});
            skPoint(sketch, "E219.visualSharp", {"position": v(-5, 55) * mm});
            skArc(sketch, "E219.filletArc", {"start": v(-1.5, 55) * mm, "mid": v(-3.97, 53.97) * mm, "end": v(-5, 51.5) * mm});
            skPoint(sketch, "E220.visualSharp", {"position": v(5, 55) * mm});
            skArc(sketch, "E220.filletArc", {"start": v(5, 51.5) * mm, "mid": v(3.97, 53.97) * mm, "end": v(1.5, 55) * mm});
            skLineSegment(sketch, "E221.1.0", {"start": v(-37.3, 30.22) * mm, "end": v(-39.95, 32.88) * mm});
            skArc(sketch, "E221.1.1", {"start": v(-39.95, 37.83) * mm, "mid": v(-40.98, 35.36) * mm, "end": v(-39.95, 32.88) * mm});
            skLineSegment(sketch, "E221.1.2", {"start": v(-39.95, 37.83) * mm, "end": v(-37.83, 39.95) * mm});
            skArc(sketch, "E221.1.3", {"start": v(-32.88, 39.95) * mm, "mid": v(-35.36, 40.98) * mm, "end": v(-37.83, 39.95) * mm});
            skLineSegment(sketch, "E221.1.4", {"start": v(-32.88, 39.95) * mm, "end": v(-30.22, 37.3) * mm});
            skArc(sketch, "E221.1.5", {"start": v(-30.22, 37.3) * mm, "mid": v(-33.94, 33.94) * mm, "end": v(-37.3, 30.22) * mm});
            skLineSegment(sketch, "E221.2.0", {"start": v(-47.74, -5) * mm, "end": v(-51.5, -5) * mm});
            skArc(sketch, "E221.2.1", {"start": v(-55, -1.5) * mm, "mid": v(-53.97, -3.97) * mm, "end": v(-51.5, -5) * mm});
            skLineSegment(sketch, "E221.2.2", {"start": v(-55, -1.5) * mm, "end": v(-55, 1.5) * mm});
            skArc(sketch, "E221.2.3", {"start": v(-51.5, 5) * mm, "mid": v(-53.97, 3.97) * mm, "end": v(-55, 1.5) * mm});
            skLineSegment(sketch, "E221.2.4", {"start": v(-51.5, 5) * mm, "end": v(-47.74, 5) * mm});
            skArc(sketch, "E221.2.5", {"start": v(-47.74, 5) * mm, "mid": v(-48, 0) * mm, "end": v(-47.74, -5) * mm});
            skLineSegment(sketch, "E221.3.0", {"start": v(-30.22, -37.3) * mm, "end": v(-32.88, -39.95) * mm});
            skArc(sketch, "E221.3.1", {"start": v(-37.83, -39.95) * mm, "mid": v(-35.36, -40.98) * mm, "end": v(-32.88, -39.95) * mm});
            skLineSegment(sketch, "E221.3.2", {"start": v(-37.83, -39.95) * mm, "end": v(-39.95, -37.83) * mm});
            skArc(sketch, "E221.3.3", {"start": v(-39.95, -32.88) * mm, "mid": v(-40.98, -35.36) * mm, "end": v(-39.95, -37.83) * mm});
            skLineSegment(sketch, "E221.3.4", {"start": v(-39.95, -32.88) * mm, "end": v(-37.3, -30.22) * mm});
            skArc(sketch, "E221.3.5", {"start": v(-37.3, -30.22) * mm, "mid": v(-33.94, -33.94) * mm, "end": v(-30.22, -37.3) * mm});
            skLineSegment(sketch, "E221.4.0", {"start": v(5, -47.74) * mm, "end": v(5, -51.5) * mm});
            skArc(sketch, "E221.4.1", {"start": v(1.5, -55) * mm, "mid": v(3.97, -53.97) * mm, "end": v(5, -51.5) * mm});
            skLineSegment(sketch, "E221.4.2", {"start": v(1.5, -55) * mm, "end": v(-1.5, -55) * mm});
            skArc(sketch, "E221.4.3", {"start": v(-5, -51.5) * mm, "mid": v(-3.97, -53.97) * mm, "end": v(-1.5, -55) * mm});
            skLineSegment(sketch, "E221.4.4", {"start": v(-5, -51.5) * mm, "end": v(-5, -47.74) * mm});
            skArc(sketch, "E221.4.5", {"start": v(-5, -47.74) * mm, "mid": v(0, -48) * mm, "end": v(5, -47.74) * mm});
            skLineSegment(sketch, "E221.5.0", {"start": v(37.3, -30.22) * mm, "end": v(39.95, -32.88) * mm});
            skArc(sketch, "E221.5.1", {"start": v(39.95, -37.83) * mm, "mid": v(40.98, -35.36) * mm, "end": v(39.95, -32.88) * mm});
            skLineSegment(sketch, "E221.5.2", {"start": v(39.95, -37.83) * mm, "end": v(37.83, -39.95) * mm});
            skArc(sketch, "E221.5.3", {"start": v(32.88, -39.95) * mm, "mid": v(35.36, -40.98) * mm, "end": v(37.83, -39.95) * mm});
            skLineSegment(sketch, "E221.5.4", {"start": v(32.88, -39.95) * mm, "end": v(30.22, -37.3) * mm});
            skArc(sketch, "E221.5.5", {"start": v(30.22, -37.3) * mm, "mid": v(33.94, -33.94) * mm, "end": v(37.3, -30.22) * mm});
            skLineSegment(sketch, "E221.6.0", {"start": v(47.74, 5) * mm, "end": v(51.5, 5) * mm});
            skArc(sketch, "E221.6.1", {"start": v(55, 1.5) * mm, "mid": v(53.97, 3.97) * mm, "end": v(51.5, 5) * mm});
            skLineSegment(sketch, "E221.6.2", {"start": v(55, 1.5) * mm, "end": v(55, -1.5) * mm});
            skArc(sketch, "E221.6.3", {"start": v(51.5, -5) * mm, "mid": v(53.97, -3.97) * mm, "end": v(55, -1.5) * mm});
            skLineSegment(sketch, "E221.6.4", {"start": v(51.5, -5) * mm, "end": v(47.74, -5) * mm});
            skArc(sketch, "E221.6.5", {"start": v(47.74, -5) * mm, "mid": v(48, 0) * mm, "end": v(47.74, 5) * mm});
            skLineSegment(sketch, "E221.7.0", {"start": v(30.22, 37.3) * mm, "end": v(32.88, 39.95) * mm});
            skArc(sketch, "E221.7.1", {"start": v(37.83, 39.95) * mm, "mid": v(35.36, 40.98) * mm, "end": v(32.88, 39.95) * mm});
            skLineSegment(sketch, "E221.7.2", {"start": v(37.83, 39.95) * mm, "end": v(39.95, 37.83) * mm});
            skArc(sketch, "E221.7.3", {"start": v(39.95, 32.88) * mm, "mid": v(40.98, 35.36) * mm, "end": v(39.95, 37.83) * mm});
            skLineSegment(sketch, "E221.7.4", {"start": v(39.95, 32.88) * mm, "end": v(37.3, 30.22) * mm});
            skArc(sketch, "E221.7.5", {"start": v(37.3, 30.22) * mm, "mid": v(33.94, 33.94) * mm, "end": v(30.22, 37.3) * mm});
            skPoint(sketch, "E222", {"position": v(0, 51.5) * mm});
            skCircle(sketch, "E223.cCircle", {"center": v(0, 51.5) * mm, "radius": 2.5 * mm, "construction": true});
            skLineSegment(sketch, "E223.0", {"start": v(0.75, 54.29) * mm, "end": v(2.8, 52.24) * mm, "construction": true});
            skLineSegment(sketch, "E223.1", {"start": v(2.8, 52.24) * mm, "end": v(2.04, 49.45) * mm, "construction": true});
            skLineSegment(sketch, "E223.2", {"start": v(2.04, 49.45) * mm, "end": v(-0.75, 48.71) * mm, "construction": true});
            skLineSegment(sketch, "E223.3", {"start": v(-0.75, 48.71) * mm, "end": v(-2.8, 50.76) * mm, "construction": true});
            skLineSegment(sketch, "E223.4", {"start": v(-2.8, 50.76) * mm, "end": v(-2.04, 53.55) * mm, "construction": true});
            skLineSegment(sketch, "E223.5", {"start": v(-2.04, 53.55) * mm, "end": v(0.75, 54.29) * mm, "construction": true});
            skPoint(sketch, "E223.0.midPoint", {"position": v(1.77, 53.26) * mm});
            skCircle(sketch, "E224", {"center": v(0, 0) * mm, "radius": 51.5 * mm, "construction": true});
            skLineSegment(sketch, "E225", {"start": v(0, 0) * mm, "end": v(-36.42, 36.42) * mm, "construction": true});
            skLineSegment(sketch, "E226.1.0", {"start": v(0, 0) * mm, "end": v(-51.5, 0) * mm, "construction": true});
            skLineSegment(sketch, "E226.2.0", {"start": v(0, 0) * mm, "end": v(-36.42, -36.42) * mm, "construction": true});
            skLineSegment(sketch, "E226.3.0", {"start": v(0, 0) * mm, "end": v(0, -51.5) * mm, "construction": true});
            skLineSegment(sketch, "E226.4.0", {"start": v(0, 0) * mm, "end": v(36.42, -36.42) * mm, "construction": true});
            skLineSegment(sketch, "E226.5.0", {"start": v(0, 0) * mm, "end": v(51.5, 0) * mm, "construction": true});
            skLineSegment(sketch, "E226.6.0", {"start": v(0, 0) * mm, "end": v(36.42, 36.42) * mm, "construction": true});
            skLineSegment(sketch, "E226.7.0", {"start": v(0, 0) * mm, "end": v(0, 51.5) * mm, "construction": true});
            skSolve(sketch);
        }
        {
            var Q0;
            Q0=qSketchRegion(id+"F22",true);
            extrude(context, id + "F23", {"entities" : qUnion([Q0]), "operationType" : NewBodyOperationType.REMOVE, "depth" : 25 * mm});
        }
        {
            var Q0;
            Q0=sQuery(id+"F22.wireOp",VERTEX,"E222");
            var Q1;
            Q1=sQuery(id+"F22.wireOp",VERTEX,"E225.end");
            var Q2;
            Q2=sQuery(id+"F22.wireOp",VERTEX,"E226.6.0.end");
            var Q3;
            Q3=sQuery(id+"F22.wireOp",VERTEX,"E226.1.0.end");
            var Q4;
            Q4=sQuery(id+"F22.wireOp",VERTEX,"E226.2.0.end");
            var Q5;
            Q5=sQuery(id+"F22.wireOp",VERTEX,"E226.3.0.end");
            var Q6;
            Q6=sQuery(id+"F22.wireOp",VERTEX,"E226.4.0.end");
            var Q7;
            Q7=sQuery(id+"F22.wireOp",VERTEX,"E226.5.0.end");
            var Q8;
            Q8=makeQuery(id+"F2.opRevolve","SWEPT_BODY",BODY,{"disambiguationData":[OSD([sQuery(id+"F1.wireOp",EDGE,"E0"),sQuery(id+"F1.wireOp",EDGE,"E1"),sQuery(id+"F1.wireOp",EDGE,"E3"),sQuery(id+"F1.wireOp",EDGE,"E4"),sQuery(id+"F1.wireOp",EDGE,"E5"),sQuery(id+"F1.wireOp",EDGE,"E6"),sQuery(id+"F1.wireOp",EDGE,"E8"),sQuery(id+"F1.wireOp",EDGE,"E10"),sQuery(id+"F1.wireOp",EDGE,"E11"),sQuery(id+"F1.wireOp",EDGE,"E12"),sQuery(id+"F1.wireOp",EDGE,"E13"),sQuery(id+"F1.wireOp",EDGE,"E14"),sQuery(id+"F1.wireOp",EDGE,"E16.MirrorCS"),sQuery(id+"F1.wireOp",EDGE,"E17.MirrorCS"),sQuery(id+"F1.wireOp",EDGE,"E18.MirrorCS"),sQuery(id+"F1.wireOp",EDGE,"E19.MirrorCS"),sQuery(id+"F1.wireOp",EDGE,"E20"),sQuery(id+"F1.wireOp",EDGE,"E22"),sQuery(id+"F1.wireOp",EDGE,"E23"),sQuery(id+"F1.wireOp",EDGE,"E24"),sQuery(id+"F1.wireOp",EDGE,"E25"),sQuery(id+"F1.wireOp",EDGE,"E26"),sQuery(id+"F1.wireOp",EDGE,"E27"),sQuery(id+"F1.wireOp",EDGE,"E28"),sQuery(id+"F1.wireOp",EDGE,"E29"),sQuery(id+"F1.wireOp",EDGE,"E30"),sQuery(id+"F1.wireOp",EDGE,"E31")])]});
            hole(context, id + "F24", {"style" : HoleStyle.SIMPLE, "endStyle" : HoleEndStyle.BLIND, "standardTappedOrClearance" : lookupTablePath({ "standard" : "ISO", "engagement" : "75%", "pitch" : "0.5 mm", "size" : "M3", "type" : "Tapped" }), "standardBlindInLast" : lookupTablePath({ "standard" : "ISO", "engagement" : "75%", "pitch" : "0.5 mm", "size" : "M3", "type" : "Tapped" }), "holeDiameter" : 2.5 * mm, "showTappedDepth" : true, "holeDepth" : (getVariable(context, 'M3_Helicoil_Drill_Depth')) * mm, "tappedDepth" : 7.5 * mm, "tapClearance" : 3, "locations" : qUnion([Q0, Q1, Q2, Q3, Q4, Q5, Q6, Q7]), "scope" : qUnion([Q8]), "majorDiameter" : 3 * mm});
        }
        {
            var Q0;
            Q0=makeQuery(id+"F2.opRevolve","SWEPT_FACE",FACE,{"disambiguationData":[OSD([sQuery(id+"F1.wireOp",EDGE,"E1")])]});
            var sketch = newSketch(context, id + "F25", { "sketchPlane" : qUnion([Q0])});
            skCircle(sketch, "E227", {"center": v(0, 0) * mm, "radius": 69.85 * mm});
            skCircle(sketch, "E228", {"center": v(0, 0) * mm, "radius": 63.5 * mm});
            skSolve(sketch);
        }
        {
            var Q0;
            Q0=qSketchRegion(id+"F25",true);
            extrude(context, id + "F26", {"entities" : qUnion([Q0]), "depth" : 150 * mm});
        }
        {
            var Q0;
            Q0=makeQuery(id+"F2.opRevolve","SWEPT_FACE",FACE,{"disambiguationData":[OSD([sQuery(id+"F1.wireOp",EDGE,"E22")])]});
            var Q1;
            Q1=sQuery(id+"F5.wireOp",VERTEX,"E40");
            cPlane(context, id + "F27", {"entities" : qUnion([Q0, Q1]), "cplaneType" : CPlaneType.PLANE_POINT, "offset" : 25 * mm, "width" : 150 * mm, "height" : 150 * mm});
        }
        {
            var Q0;
            Q0=qCreatedBy(id+"F27.planeOp",FACE);
            var sketch = newSketch(context, id + "F28", { "sketchPlane" : qUnion([Q0])});
            skCircle(sketch, "E229.0", {"center": v(0, 0) * mm, "radius": 63 * mm, "construction": true});
            skLineSegment(sketch, "E230", {"start": v(0, 0) * mm, "end": v(0, 63) * mm, "construction": true});
            skLineSegment(sketch, "E231", {"start": v(0, 0) * mm, "end": v(24.1, 58.2) * mm, "construction": true});
            skLineSegment(sketch, "E232.1.0", {"start": v(0, 0) * mm, "end": v(-24.1, 58.2) * mm, "construction": true});
            skLineSegment(sketch, "E232.2.0", {"start": v(0, 0) * mm, "end": v(-58.2, 24.1) * mm, "construction": true});
            skLineSegment(sketch, "E232.3.0", {"start": v(0, 0) * mm, "end": v(-58.2, -24.1) * mm, "construction": true});
            skLineSegment(sketch, "E232.4.0", {"start": v(0, 0) * mm, "end": v(-24.1, -58.2) * mm, "construction": true});
            skLineSegment(sketch, "E232.5.0", {"start": v(0, 0) * mm, "end": v(24.1, -58.2) * mm, "construction": true});
            skLineSegment(sketch, "E232.6.0", {"start": v(0, 0) * mm, "end": v(58.2, -24.1) * mm, "construction": true});
            skLineSegment(sketch, "E232.7.0", {"start": v(0, 0) * mm, "end": v(58.2, 24.1) * mm, "construction": true});
            skPoint(sketch, "E233", {"position": v(24.1, 58.2) * mm});
            skPoint(sketch, "E234", {"position": v(58.2, 24.1) * mm});
            skPoint(sketch, "E235", {"position": v(58.2, -24.1) * mm});
            skPoint(sketch, "E236", {"position": v(24.1, -58.2) * mm});
            skPoint(sketch, "E237", {"position": v(-24.1, -58.2) * mm});
            skPoint(sketch, "E238", {"position": v(-58.2, -24.1) * mm});
            skPoint(sketch, "E239", {"position": v(-58.2, 24.1) * mm});
            skPoint(sketch, "E240", {"position": v(-24.1, 58.2) * mm});
            skSolve(sketch);
        }
        {
            var Q0;
            Q0=sQuery(id+"F28.wireOp",VERTEX,"E233");
            var Q1;
            Q1=sQuery(id+"F28.wireOp",EDGE,"E231");
            cPlane(context, id + "F29", {"entities" : qUnion([Q0, Q1]), "cplaneType" : CPlaneType.LINE_POINT, "offset" : 25 * mm, "width" : 150 * mm, "height" : 150 * mm});
        }
        {
            var Q0;
            Q0=sQuery(id+"F28.wireOp",EDGE,"E232.7.0");
            var Q1;
            Q1=sQuery(id+"F28.wireOp",VERTEX,"E234");
            cPlane(context, id + "F30", {"entities" : qUnion([Q0, Q1]), "cplaneType" : CPlaneType.LINE_POINT, "offset" : 25 * mm, "width" : 150 * mm, "height" : 150 * mm});
        }
        {
            var Q0;
            Q0=sQuery(id+"F28.wireOp",EDGE,"E232.6.0");
            var Q1;
            Q1=sQuery(id+"F28.wireOp",VERTEX,"E235");
            cPlane(context, id + "F31", {"entities" : qUnion([Q0, Q1]), "cplaneType" : CPlaneType.LINE_POINT, "offset" : 25 * mm, "width" : 150 * mm, "height" : 150 * mm});
        }
        {
            var Q0;
            Q0=sQuery(id+"F28.wireOp",EDGE,"E232.5.0");
            var Q1;
            Q1=sQuery(id+"F28.wireOp",VERTEX,"E236");
            cPlane(context, id + "F32", {"entities" : qUnion([Q0, Q1]), "cplaneType" : CPlaneType.LINE_POINT, "offset" : 25 * mm, "width" : 150 * mm, "height" : 150 * mm});
        }
        {
            var Q0;
            Q0=sQuery(id+"F28.wireOp",EDGE,"E232.4.0");
            var Q1;
            Q1=sQuery(id+"F28.wireOp",VERTEX,"E237");
            cPlane(context, id + "F33", {"entities" : qUnion([Q0, Q1]), "cplaneType" : CPlaneType.LINE_POINT, "offset" : 25 * mm, "width" : 150 * mm, "height" : 150 * mm});
        }
        {
            var Q0;
            Q0=sQuery(id+"F28.wireOp",VERTEX,"E238");
            var Q1;
            Q1=sQuery(id+"F28.wireOp",EDGE,"E232.3.0");
            cPlane(context, id + "F34", {"entities" : qUnion([Q0, Q1]), "cplaneType" : CPlaneType.LINE_POINT, "offset" : 25 * mm, "width" : 150 * mm, "height" : 150 * mm});
        }
        {
            var Q0;
            Q0=sQuery(id+"F28.wireOp",VERTEX,"E239");
            var Q1;
            Q1=sQuery(id+"F28.wireOp",EDGE,"E232.2.0");
            cPlane(context, id + "F35", {"entities" : qUnion([Q0, Q1]), "cplaneType" : CPlaneType.LINE_POINT, "offset" : 25 * mm, "width" : 150 * mm, "height" : 150 * mm});
        }
        {
            var Q0;
            Q0=sQuery(id+"F28.wireOp",EDGE,"E232.1.0");
            var Q1;
            Q1=sQuery(id+"F28.wireOp",VERTEX,"E240");
            cPlane(context, id + "F36", {"entities" : qUnion([Q0, Q1]), "cplaneType" : CPlaneType.LINE_POINT, "offset" : 25 * mm, "width" : 150 * mm, "height" : 150 * mm});
        }
        {
            var Q0;
            Q0=qCreatedBy(id+"F29.planeOp",FACE);
            var sketch = newSketch(context, id + "F37", { "sketchPlane" : qUnion([Q0])});
            skPoint(sketch, "E241.0", {"position": v(15.25, 0) * mm});
            skSolve(sketch);
        }
        {
            var Q0;
            Q0=qCreatedBy(id+"F30.planeOp",FACE);
            var sketch = newSketch(context, id + "F38", { "sketchPlane" : qUnion([Q0])});
            skPoint(sketch, "E242.0", {"position": v(15.25, 0) * mm});
            skSolve(sketch);
        }
        {
            var Q0;
            Q0=qCreatedBy(id+"F31.planeOp",FACE);
            var sketch = newSketch(context, id + "F39", { "sketchPlane" : qUnion([Q0])});
            skPoint(sketch, "E243.0", {"position": v(15.25, 0) * mm});
            skSolve(sketch);
        }
        {
            var Q0;
            Q0=qCreatedBy(id+"F32.planeOp",FACE);
            var sketch = newSketch(context, id + "F40", { "sketchPlane" : qUnion([Q0])});
            skPoint(sketch, "E244.0", {"position": v(15.25, 0) * mm});
            skSolve(sketch);
        }
        {
            var Q0;
            Q0=qCreatedBy(id+"F33.planeOp",FACE);
            var sketch = newSketch(context, id + "F41", { "sketchPlane" : qUnion([Q0])});
            skPoint(sketch, "E245.0", {"position": v(15.25, 0) * mm});
            skSolve(sketch);
        }
        {
            var Q0;
            Q0=qCreatedBy(id+"F34.planeOp",FACE);
            var sketch = newSketch(context, id + "F42", { "sketchPlane" : qUnion([Q0])});
            skPoint(sketch, "E246.0", {"position": v(-15.25, 0) * mm});
            skSolve(sketch);
        }
        {
            var Q0;
            Q0=qCreatedBy(id+"F35.planeOp",FACE);
            var sketch = newSketch(context, id + "F43", { "sketchPlane" : qUnion([Q0])});
            skPoint(sketch, "E247.0", {"position": v(-15.25, 0) * mm});
            skSolve(sketch);
        }
        {
            var Q0;
            Q0=qCreatedBy(id+"F36.planeOp",FACE);
            var sketch = newSketch(context, id + "F44", { "sketchPlane" : qUnion([Q0])});
            skPoint(sketch, "E248.0", {"position": v(15.25, 0) * mm});
            skSolve(sketch);
        }
        {
            var Q0;
            Q0=sQuery(id+"F37.wireOp",VERTEX,"E241.0");
            var Q1;
            Q1=sQuery(id+"F43.wireOp",VERTEX,"E247.0");
            var Q2;
            Q2=sQuery(id+"F42.wireOp",VERTEX,"E246.0");
            var Q3;
            Q3=sQuery(id+"F41.wireOp",VERTEX,"E245.0");
            var Q4;
            Q4=sQuery(id+"F40.wireOp",VERTEX,"E244.0");
            var Q5;
            Q5=sQuery(id+"F39.wireOp",VERTEX,"E243.0");
            var Q6;
            Q6=sQuery(id+"F38.wireOp",VERTEX,"E242.0");
            var Q7;
            Q7=sQuery(id+"F44.wireOp",VERTEX,"E248.0");
            var Q8;
            Q8=makeQuery(id+"F2.opRevolve","SWEPT_BODY",BODY,{"disambiguationData":[OSD([sQuery(id+"F1.wireOp",EDGE,"E0"),sQuery(id+"F1.wireOp",EDGE,"E1"),sQuery(id+"F1.wireOp",EDGE,"E3"),sQuery(id+"F1.wireOp",EDGE,"E4"),sQuery(id+"F1.wireOp",EDGE,"E5"),sQuery(id+"F1.wireOp",EDGE,"E6"),sQuery(id+"F1.wireOp",EDGE,"E8"),sQuery(id+"F1.wireOp",EDGE,"E10"),sQuery(id+"F1.wireOp",EDGE,"E11"),sQuery(id+"F1.wireOp",EDGE,"E12"),sQuery(id+"F1.wireOp",EDGE,"E13"),sQuery(id+"F1.wireOp",EDGE,"E14"),sQuery(id+"F1.wireOp",EDGE,"E16.MirrorCS"),sQuery(id+"F1.wireOp",EDGE,"E17.MirrorCS"),sQuery(id+"F1.wireOp",EDGE,"E18.MirrorCS"),sQuery(id+"F1.wireOp",EDGE,"E19.MirrorCS"),sQuery(id+"F1.wireOp",EDGE,"E20"),sQuery(id+"F1.wireOp",EDGE,"E22"),sQuery(id+"F1.wireOp",EDGE,"E23"),sQuery(id+"F1.wireOp",EDGE,"E24"),sQuery(id+"F1.wireOp",EDGE,"E25"),sQuery(id+"F1.wireOp",EDGE,"E26"),sQuery(id+"F1.wireOp",EDGE,"E27"),sQuery(id+"F1.wireOp",EDGE,"E28"),sQuery(id+"F1.wireOp",EDGE,"E29"),sQuery(id+"F1.wireOp",EDGE,"E30"),sQuery(id+"F1.wireOp",EDGE,"E31")])]});
            hole(context, id + "F45", {"style" : HoleStyle.SIMPLE, "endStyle" : HoleEndStyle.BLIND, "standardTappedOrClearance" : lookupTablePath({ "standard" : "ISO", "engagement" : "75%", "pitch" : "0.5 mm", "size" : "M3", "type" : "Tapped" }), "standardBlindInLast" : lookupTablePath({ "standard" : "ISO", "engagement" : "75%", "pitch" : "0.5 mm", "size" : "M3", "type" : "Tapped" }), "holeDiameter" : 2.5 * mm, "showTappedDepth" : true, "holeDepth" : (getVariable(context, 'M3_Helicoil_Drill_Depth')) * mm, "tappedDepth" : 7.5 * mm, "tapClearance" : 3, "locations" : qUnion([Q0, Q1, Q2, Q3, Q4, Q5, Q6, Q7]), "scope" : qUnion([Q8]), "majorDiameter" : 3 * mm});
        }
        {
            var Q0;
            Q0=makeQuery(id+"F23.boolean.opBoolean","COPY",FACE,{"derivedFrom":makeQuery(id+"F23.opExtrude","CAP_FACE",FACE,{"disambiguationData":[OSD([sQuery(id+"F22.wireOp",EDGE,"E214.0"),sQuery(id+"F22.wireOp",EDGE,"E215"),sQuery(id+"F22.wireOp",EDGE,"E216"),sQuery(id+"F22.wireOp",EDGE,"E217"),sQuery(id+"F22.wireOp",EDGE,"E219.filletArc"),sQuery(id+"F22.wireOp",EDGE,"E220.filletArc")])],"isStart":true})});
            var sketch = newSketch(context, id + "F46", { "sketchPlane" : qUnion([Q0])});
            skCircle(sketch, "E249.cCircle", {"center": v(0, 51.5) * mm, "radius": 2.5 * mm, "construction": true});
            skLineSegment(sketch, "E249.0", {"start": v(2.87, 51.8) * mm, "end": v(1.7, 49.17) * mm});
            skLineSegment(sketch, "E249.1", {"start": v(1.7, 49.17) * mm, "end": v(-1.17, 48.86) * mm});
            skLineSegment(sketch, "E249.2", {"start": v(-1.17, 48.86) * mm, "end": v(-2.87, 51.2) * mm});
            skLineSegment(sketch, "E249.3", {"start": v(-2.87, 51.2) * mm, "end": v(-1.7, 53.83) * mm});
            skLineSegment(sketch, "E249.4", {"start": v(-1.7, 53.83) * mm, "end": v(1.17, 54.14) * mm});
            skLineSegment(sketch, "E249.5", {"start": v(1.17, 54.14) * mm, "end": v(2.87, 51.8) * mm});
            skPoint(sketch, "E249.0.midPoint", {"position": v(2.28, 50.48) * mm});
            skSolve(sketch);
        }
        {
            var Q0;
            Q0=qSketchRegion(id+"F46",true);
            extrude(context, id + "F47", {"entities" : qUnion([Q0]), "depth" : 20 * mm});
        }
    });
